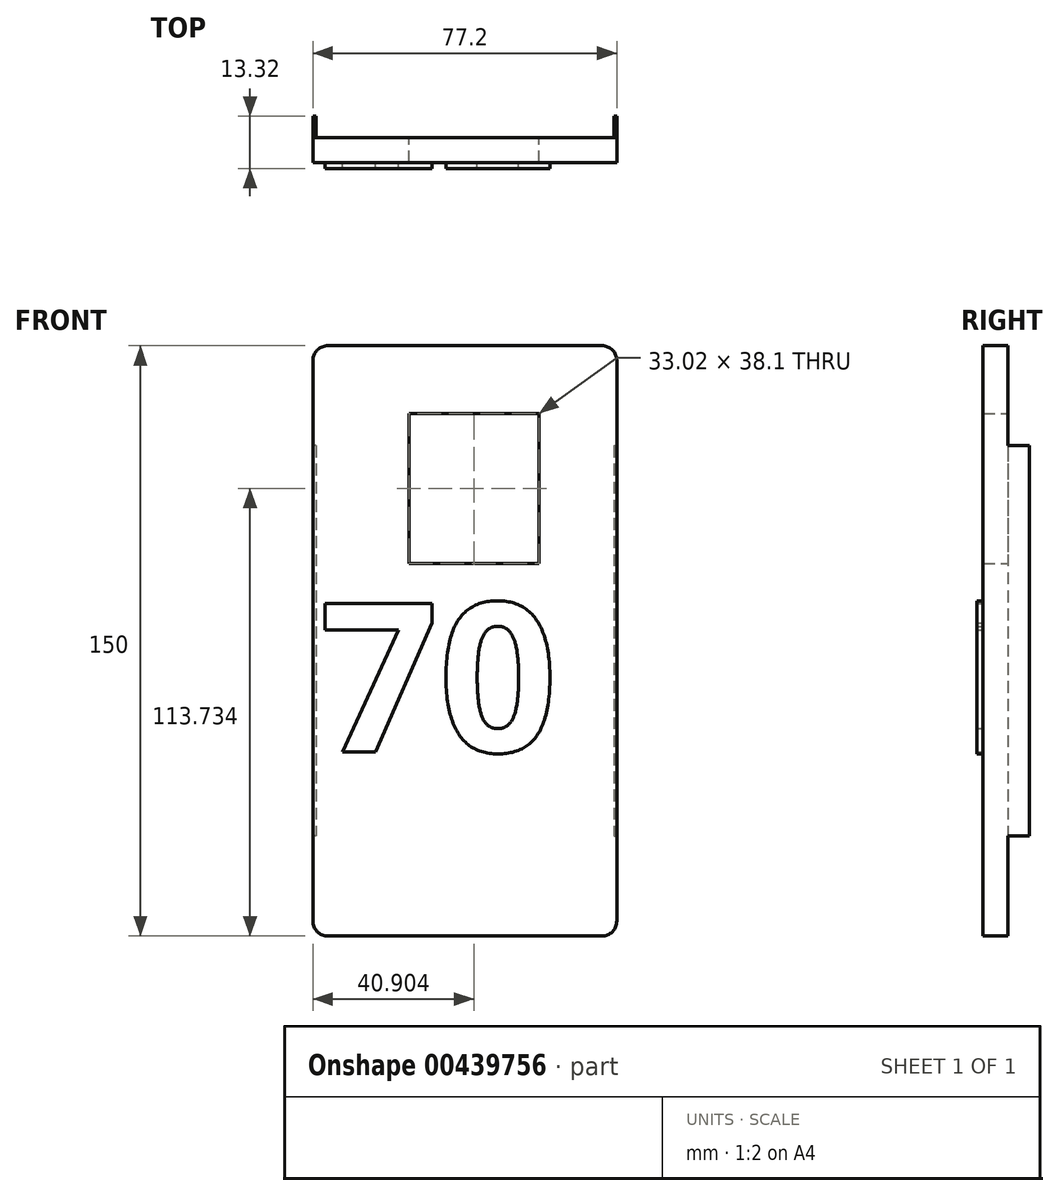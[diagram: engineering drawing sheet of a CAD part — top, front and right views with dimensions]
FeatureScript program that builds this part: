
annotation { "Feature Type Name" : "Feature", "Feature Type Description" : "" }
export const myFeature = defineFeature(function(context is Context, id is Id, definition is map)
    precondition{}
    {
        {
            var Q0;
            Q0=qCreatedBy(makeId("Front.planeOp"),FACE);
            var sketch = newSketch(context, id + "F0", { "sketchPlane" : qUnion([Q0])});
            skLineSegment(sketch, "E0.bottom", {"start": v(-14.95, 103.96) * mm, "end": v(54.65, 103.96) * mm});
            skLineSegment(sketch, "E0.top", {"start": v(-14.95, -46.04) * mm, "end": v(54.65, -46.04) * mm});
            skLineSegment(sketch, "E0.left", {"start": v(-18.75, 100.16) * mm, "end": v(-18.75, -42.24) * mm});
            skLineSegment(sketch, "E0.right", {"start": v(58.45, 100.16) * mm, "end": v(58.45, -42.24) * mm});
            skPoint(sketch, "E1.visualSharp", {"position": v(58.45, 103.96) * mm});
            skArc(sketch, "E1.filletArc", {"start": v(58.45, 100.16) * mm, "mid": v(57.33, 102.85) * mm, "end": v(54.65, 103.96) * mm});
            skPoint(sketch, "E2.visualSharp", {"position": v(-18.75, 103.96) * mm});
            skArc(sketch, "E2.filletArc", {"start": v(-14.95, 103.96) * mm, "mid": v(-17.64, 102.85) * mm, "end": v(-18.75, 100.16) * mm});
            skPoint(sketch, "E3.visualSharp", {"position": v(58.45, -46.04) * mm});
            skArc(sketch, "E3.filletArc", {"start": v(54.65, -46.04) * mm, "mid": v(57.33, -44.93) * mm, "end": v(58.45, -42.24) * mm});
            skPoint(sketch, "E4.visualSharp", {"position": v(-18.75, -46.04) * mm});
            skArc(sketch, "E4.filletArc", {"start": v(-18.75, -42.24) * mm, "mid": v(-17.64, -44.93) * mm, "end": v(-14.95, -46.04) * mm});
            skLineSegment(sketch, "E5.bottom", {"start": v(5.64, 86.74) * mm, "end": v(38.66, 86.74) * mm});
            skLineSegment(sketch, "E5.top", {"start": v(5.64, 48.64) * mm, "end": v(38.66, 48.64) * mm});
            skLineSegment(sketch, "E5.left", {"start": v(5.64, 86.74) * mm, "end": v(5.64, 48.64) * mm});
            skLineSegment(sketch, "E5.right", {"start": v(38.66, 86.74) * mm, "end": v(38.66, 48.64) * mm});
            skSolve(sketch);
        }
        {
            var Q0;
            Q0 = qSketchRegion(id + "F0", true);
            extrude(context, id + "F1", {"entities" : qUnion([Q0]), "endBound" : BoundingType.SYMMETRIC, "depth" : 6.35 * mm});
        }
        {
            var Q0;
            Q0=makeQuery(id+"F1.opExtrude","SWEPT_FACE",FACE,{"disambiguationData":[OSD([sQuery(id+"F0.wireOp",EDGE,"E0.left")])]});
            var sketch = newSketch(context, id + "F2", { "sketchPlane" : qUnion([Q0])});
            skLineSegment(sketch, "E6", {"start": v(-3.18, -20.64) * mm, "end": v(-8.62, -20.64) * mm});
            skLineSegment(sketch, "E7", {"start": v(-8.62, -20.64) * mm, "end": v(-8.62, 78.56) * mm});
            skLineSegment(sketch, "E8", {"start": v(-8.62, 78.56) * mm, "end": v(-3.18, 78.56) * mm});
            skLineSegment(sketch, "E9", {"start": v(-3.18, 78.56) * mm, "end": v(-3.18, -20.64) * mm});
            skSolve(sketch);
        }
        {
            var Q0;
            Q0=makeQuery(id+"F2.imprint","IMPRINT",FACE,{"disambiguationData":[TD([[makeQuery(id+"F2.imprint","IMPRINT",EDGE,{"derivedFrom":sQuery(id+"F2.wireOp",EDGE,"E6")}),-1.0]])]});
            extrude(context, id + "F3", {"entities" : qUnion([Q0]), "operationType" : NewBodyOperationType.ADD, "oppositeDirection" : true, "depth" : 0.76 * mm});
        }
        {
            var Q0;
            Q0=makeQuery(id+"F1.opExtrude","SWEPT_FACE",FACE,{"disambiguationData":[OSD([sQuery(id+"F0.wireOp",EDGE,"E0.right")])]});
            var sketch = newSketch(context, id + "F4", { "sketchPlane" : qUnion([Q0])});
            skLineSegment(sketch, "E10", {"start": v(3.18, 78.56) * mm, "end": v(8.61, 78.56) * mm});
            skLineSegment(sketch, "E11", {"start": v(8.61, 78.56) * mm, "end": v(8.61, -20.64) * mm});
            skLineSegment(sketch, "E12", {"start": v(8.61, -20.64) * mm, "end": v(3.18, -20.64) * mm});
            skLineSegment(sketch, "E13", {"start": v(3.18, -20.64) * mm, "end": v(3.18, 78.56) * mm});
            skSolve(sketch);
        }
        {
            var Q0;
            Q0 = qSketchRegion(id + "F4", true);
            extrude(context, id + "F5", {"entities" : qUnion([Q0]), "operationType" : NewBodyOperationType.ADD, "oppositeDirection" : true, "depth" : 0.76 * mm});
        }
        {
            var Q0;
            Q0=makeQuery(id+"F1.opExtrude","CAP_FACE",FACE,{"disambiguationData":[OSD([sQuery(id+"F0.wireOp",EDGE,"E0.bottom"),sQuery(id+"F0.wireOp",EDGE,"E0.top"),sQuery(id+"F0.wireOp",EDGE,"E0.left"),sQuery(id+"F0.wireOp",EDGE,"E0.right"),sQuery(id+"F0.wireOp",EDGE,"E1.filletArc"),sQuery(id+"F0.wireOp",EDGE,"E2.filletArc"),sQuery(id+"F0.wireOp",EDGE,"E3.filletArc"),sQuery(id+"F0.wireOp",EDGE,"E4.filletArc"),sQuery(id+"F0.wireOp",EDGE,"E5.bottom"),sQuery(id+"F0.wireOp",EDGE,"E5.top"),sQuery(id+"F0.wireOp",EDGE,"E5.left"),sQuery(id+"F0.wireOp",EDGE,"E5.right")])],"isStart":false});
            var sketch = newSketch(context, id + "F6", { "sketchPlane" : qUnion([Q0])});
            skText(sketch, "E14", { "text": "70", "fontName": "OpenSans-Bold.ttf"});
            const initialGuessF6  = {"E14": [-0.01707, 0.00076, 1, 0, 0.0381]};
            skSetInitialGuess(sketch, initialGuessF6);
            skSolve(sketch);
        }
        {
            var Q0;
            Q0=makeQuery(id+"F6.imprint","IMPRINT",FACE,{"disambiguationData":[TD([[makeQuery(id+"F6.imprint","IMPRINT",EDGE,{"derivedFrom":sQuery(id+"F6.wireOp",EDGE,"E14.sketch_text.stroke-7")}),-1.0]])]});
            var Q1;
            Q1=makeQuery(id+"F6.imprint","IMPRINT",FACE,{"disambiguationData":[TD([[makeQuery(id+"F6.imprint","IMPRINT",EDGE,{"derivedFrom":sQuery(id+"F6.wireOp",EDGE,"E14.sketch_text.stroke-0")}),-1.0]])]});
            extrude(context, id + "F7", {"entities" : qUnion([Q0, Q1]), "operationType" : NewBodyOperationType.ADD, "depth" : 1.52 * mm});
        }
    });
